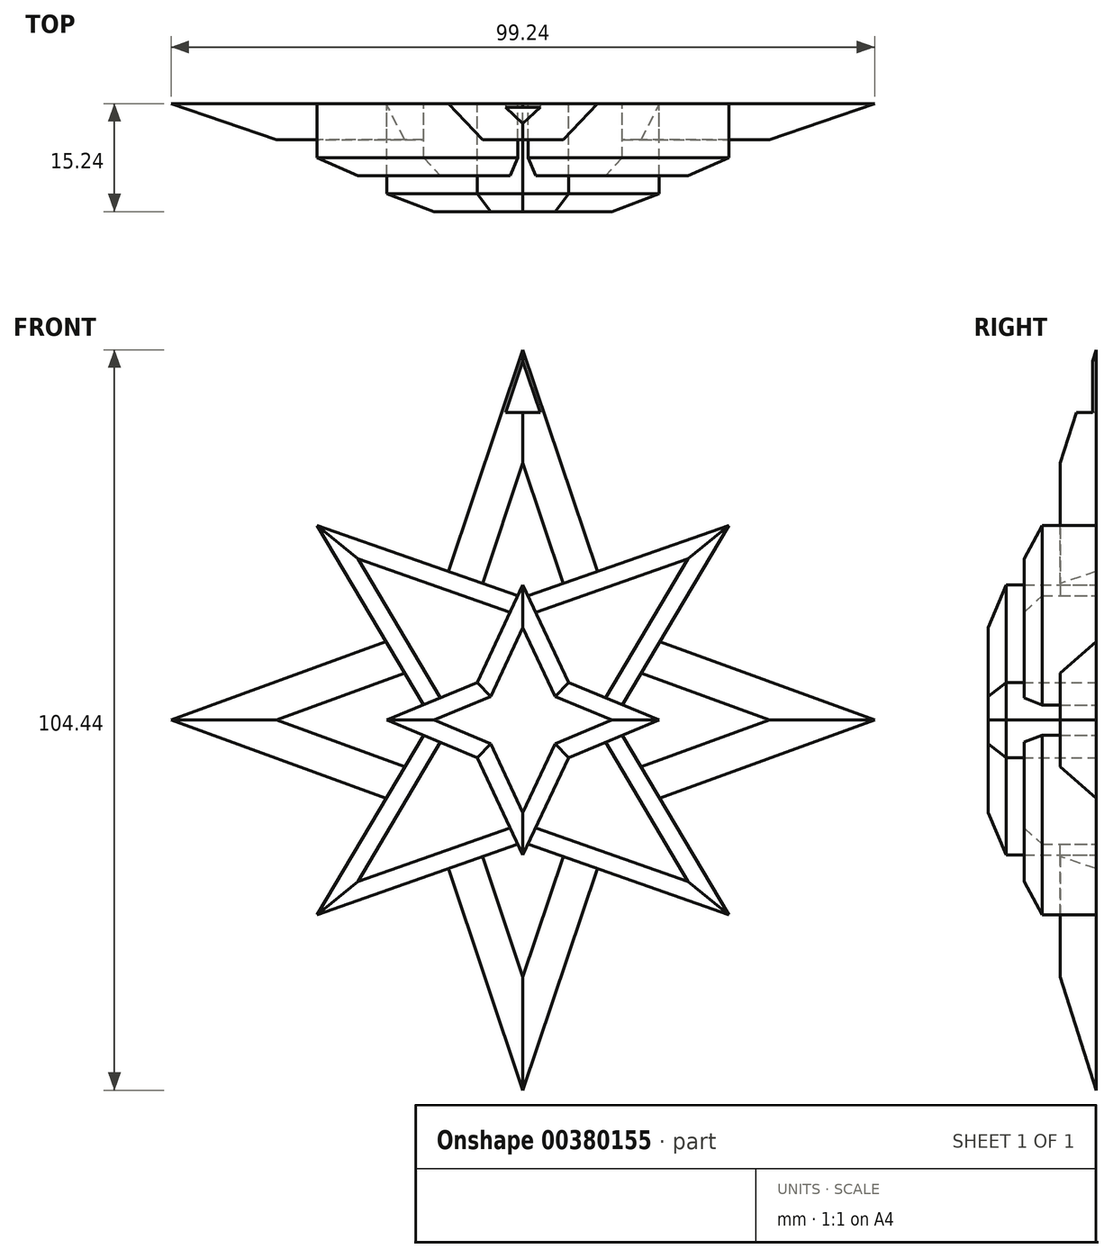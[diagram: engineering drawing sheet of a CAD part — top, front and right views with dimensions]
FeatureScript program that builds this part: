
annotation { "Feature Type Name" : "Feature", "Feature Type Description" : "" }
export const myFeature = defineFeature(function(context is Context, id is Id, definition is map)
    precondition{}
    {
        {
            var Q0;
            Q0=qCreatedBy(makeId("Front.planeOp"),FACE);
            var sketch = newSketch(context, id + "F0", { "sketchPlane" : qUnion([Q0])});
            skLineSegment(sketch, "E0", {"start": v(-49.62, 0) * mm, "end": v(-19.3, 11.04) * mm});
            skLineSegment(sketch, "E1", {"start": v(-19.3, 11.04) * mm, "end": v(-29.04, 27.46) * mm});
            skLineSegment(sketch, "E2", {"start": v(-29.04, 27.46) * mm, "end": v(-10.5, 20.95) * mm});
            skLineSegment(sketch, "E3", {"start": v(-10.5, 20.95) * mm, "end": v(0, 52.22) * mm});
            skLineSegment(sketch, "E4.MirrorCS", {"start": v(10.5, 20.95) * mm, "end": v(0, 52.22) * mm});
            skLineSegment(sketch, "E5.MirrorCS", {"start": v(29.04, 27.46) * mm, "end": v(10.5, 20.95) * mm});
            skLineSegment(sketch, "E6.MirrorCS", {"start": v(19.3, 11.04) * mm, "end": v(29.04, 27.46) * mm});
            skLineSegment(sketch, "E7.MirrorCS", {"start": v(49.62, 0) * mm, "end": v(19.3, 11.04) * mm});
            skLineSegment(sketch, "E8.MirrorCS", {"start": v(-49.62, 0) * mm, "end": v(-19.3, -11.04) * mm});
            skLineSegment(sketch, "E9.MirrorCS", {"start": v(-19.3, -11.04) * mm, "end": v(-29.04, -27.46) * mm});
            skLineSegment(sketch, "E10.MirrorCS", {"start": v(-29.04, -27.46) * mm, "end": v(-10.5, -20.95) * mm});
            skLineSegment(sketch, "E11.MirrorCS", {"start": v(-10.5, -20.95) * mm, "end": v(0, -52.22) * mm});
            skLineSegment(sketch, "E12.MirrorCS", {"start": v(10.5, -20.95) * mm, "end": v(0, -52.22) * mm});
            skLineSegment(sketch, "E13.MirrorCS", {"start": v(29.04, -27.46) * mm, "end": v(10.5, -20.95) * mm});
            skLineSegment(sketch, "E14.MirrorCS", {"start": v(19.3, -11.04) * mm, "end": v(29.04, -27.46) * mm});
            skLineSegment(sketch, "E15.MirrorCS", {"start": v(49.62, 0) * mm, "end": v(19.3, -11.04) * mm});
            skLineSegment(sketch, "E16", {"start": v(0, 19.05) * mm, "end": v(-6.42, 5.3) * mm});
            skLineSegment(sketch, "E17", {"start": v(-6.42, 5.3) * mm, "end": v(-19.2, 0) * mm});
            skLineSegment(sketch, "E18.MirrorCS", {"start": v(6.42, 5.3) * mm, "end": v(19.2, 0) * mm});
            skLineSegment(sketch, "E19.MirrorCS", {"start": v(0, 19.05) * mm, "end": v(6.42, 5.3) * mm});
            skLineSegment(sketch, "E20.MirrorCS", {"start": v(6.42, -5.3) * mm, "end": v(19.2, 0) * mm});
            skLineSegment(sketch, "E21.MirrorCS", {"start": v(0, -19.05) * mm, "end": v(6.42, -5.3) * mm});
            skLineSegment(sketch, "E22.MirrorCS", {"start": v(0, -19.05) * mm, "end": v(-6.42, -5.3) * mm});
            skLineSegment(sketch, "E23.MirrorCS", {"start": v(-6.42, -5.3) * mm, "end": v(-19.2, 0) * mm});
            skLineSegment(sketch, "E24", {"start": v(-19.3, 11.04) * mm, "end": v(-14.03, 2.14) * mm});
            skLineSegment(sketch, "E25", {"start": v(-10.5, 20.95) * mm, "end": v(-0.71, 17.52) * mm});
            skLineSegment(sketch, "E26", {"start": v(-19.3, -11.04) * mm, "end": v(-14.03, -2.14) * mm});
            skLineSegment(sketch, "E27", {"start": v(-10.5, -20.95) * mm, "end": v(-0.71, -17.52) * mm});
            skLineSegment(sketch, "E28", {"start": v(10.5, 20.95) * mm, "end": v(0.71, 17.52) * mm});
            skLineSegment(sketch, "E29", {"start": v(19.3, 11.04) * mm, "end": v(14.03, 2.14) * mm});
            skLineSegment(sketch, "E30", {"start": v(10.5, -20.95) * mm, "end": v(0.71, -17.52) * mm});
            skLineSegment(sketch, "E31", {"start": v(19.3, -11.04) * mm, "end": v(14.03, -2.14) * mm});
            skLineSegment(sketch, "E32", {"start": v(-49.62, 0) * mm, "end": v(-19.2, 0) * mm});
            skLineSegment(sketch, "E33", {"start": v(0, 19.05) * mm, "end": v(0, 52.22) * mm});
            skLineSegment(sketch, "E34", {"start": v(19.2, 0) * mm, "end": v(49.62, 0) * mm});
            skLineSegment(sketch, "E35", {"start": v(0, -19.05) * mm, "end": v(0, -52.22) * mm});
            skSolve(sketch);
        }
        {
            var Q0;
            Q0=makeQuery(id+"F0.imprint","IMPRINT",FACE,{"disambiguationData":[TD([[makeQuery(id+"F0.imprint","IMPRINT",EDGE,{"derivedFrom":sQuery(id+"F0.wireOp",EDGE,"E8.MirrorCS")}),1.0]])]});
            var Q1;
            Q1=makeQuery(id+"F0.imprint","IMPRINT",FACE,{"disambiguationData":[TD([[makeQuery(id+"F0.imprint","IMPRINT",EDGE,{"derivedFrom":sQuery(id+"F0.wireOp",EDGE,"E0")}),-1.0]])]});
            var Q2;
            Q2=makeQuery(id+"F0.imprint","IMPRINT",FACE,{"disambiguationData":[TD([[makeQuery(id+"F0.imprint","IMPRINT",EDGE,{"derivedFrom":sQuery(id+"F0.wireOp",EDGE,"E4.MirrorCS")}),1.0]])]});
            var Q3;
            Q3=makeQuery(id+"F0.imprint","IMPRINT",FACE,{"disambiguationData":[TD([[makeQuery(id+"F0.imprint","IMPRINT",EDGE,{"derivedFrom":sQuery(id+"F0.wireOp",EDGE,"E7.MirrorCS")}),1.0]])]});
            var Q4;
            Q4=makeQuery(id+"F0.imprint","IMPRINT",FACE,{"disambiguationData":[TD([[makeQuery(id+"F0.imprint","IMPRINT",EDGE,{"derivedFrom":sQuery(id+"F0.wireOp",EDGE,"E15.MirrorCS")}),-1.0]])]});
            var Q5;
            Q5=makeQuery(id+"F0.imprint","IMPRINT",FACE,{"disambiguationData":[TD([[makeQuery(id+"F0.imprint","IMPRINT",EDGE,{"derivedFrom":sQuery(id+"F0.wireOp",EDGE,"E3")}),-1.0]])]});
            var Q6;
            Q6=makeQuery(id+"F0.imprint","IMPRINT",FACE,{"disambiguationData":[TD([[makeQuery(id+"F0.imprint","IMPRINT",EDGE,{"derivedFrom":sQuery(id+"F0.wireOp",EDGE,"E12.MirrorCS")}),-1.0]])]});
            var Q7;
            Q7=makeQuery(id+"F0.imprint","IMPRINT",FACE,{"disambiguationData":[TD([[makeQuery(id+"F0.imprint","IMPRINT",EDGE,{"derivedFrom":sQuery(id+"F0.wireOp",EDGE,"E11.MirrorCS")}),1.0]])]});
            extrude(context, id + "F1", {"entities" : qUnion([Q0, Q1, Q2, Q3, Q4, Q5, Q6, Q7]), "depth" : 5.08 * mm});
        }
        {
            var Q0;
            Q0=makeQuery(id+"F0.imprint","IMPRINT",FACE,{"disambiguationData":[TD([[makeQuery(id+"F0.imprint","IMPRINT",EDGE,{"derivedFrom":sQuery(id+"F0.wireOp",EDGE,"E1")}),-1.0]])]});
            var Q1;
            Q1=makeQuery(id+"F0.imprint","IMPRINT",FACE,{"disambiguationData":[TD([[makeQuery(id+"F0.imprint","IMPRINT",EDGE,{"derivedFrom":sQuery(id+"F0.wireOp",EDGE,"E9.MirrorCS")}),1.0]])]});
            var Q2;
            Q2=makeQuery(id+"F0.imprint","IMPRINT",FACE,{"disambiguationData":[TD([[makeQuery(id+"F0.imprint","IMPRINT",EDGE,{"derivedFrom":sQuery(id+"F0.wireOp",EDGE,"E13.MirrorCS")}),-1.0]])]});
            var Q3;
            Q3=makeQuery(id+"F0.imprint","IMPRINT",FACE,{"disambiguationData":[TD([[makeQuery(id+"F0.imprint","IMPRINT",EDGE,{"derivedFrom":sQuery(id+"F0.wireOp",EDGE,"E5.MirrorCS")}),1.0]])]});
            extrude(context, id + "F2", {"entities" : qUnion([Q0, Q1, Q2, Q3]), "depth" : 10.16 * mm});
        }
        {
            var Q0;
            {var subQ9=sQuery(id+"F0.wireOp",EDGE,"E16");var subQ13=sQuery(id+"F0.wireOp",EDGE,"E17");var subQ14=makeQuery(id+"F0.imprint","INTERSECT",VERTEX,{"derivedFrom":[subQ9,subQ13]});Q0=makeQuery(id+"F0.imprint","IMPRINT",FACE,{"disambiguationData":[TD([[makeQuery(id+"F0.imprint","IMPRINT",EDGE,{"disambiguationData":[TD([[subQ14,1.0]])],"derivedFrom":subQ9}),1.0]])]});}
            extrude(context, id + "F3", {"entities" : qUnion([Q0]), "depth" : 15.24 * mm});
        }
        {
            var Q0;
            Q0=makeQuery(id+"F1.opExtrude","CAP_FACE",FACE,{"disambiguationData":[OSD([sQuery(id+"F0.wireOp",EDGE,"E3"),sQuery(id+"F0.wireOp",EDGE,"E4.MirrorCS"),sQuery(id+"F0.wireOp",EDGE,"E16"),sQuery(id+"F0.wireOp",EDGE,"E19.MirrorCS"),sQuery(id+"F0.wireOp",EDGE,"E25"),sQuery(id+"F0.wireOp",EDGE,"E28")])],"isStart":false});
            var sketch = newSketch(context, id + "F4", { "sketchPlane" : qUnion([Q0])});
            skLineSegment(sketch, "E36", {"start": v(0, 50.61) * mm, "end": v(-2.43, 43.39) * mm});
            skLineSegment(sketch, "E37.MirrorCS", {"start": v(0, 50.61) * mm, "end": v(2.43, 43.39) * mm});
            skLineSegment(sketch, "E38", {"start": v(-2.43, 43.39) * mm, "end": v(2.43, 43.39) * mm});
            skSolve(sketch);
        }
        {
            var Q0;
            Q0 = qSketchRegion(id + "F4", true);
            extrude(context, id + "F5", {"entities" : qUnion([Q0]), "operationType" : NewBodyOperationType.REMOVE, "oppositeDirection" : true, "depth" : 25.4 * mm});
        }
        {
            var Q0;
            Q0=makeQuery(id+"F2.opExtrude","CAP_EDGE",EDGE,{"disambiguationData":[OSD([sQuery(id+"F0.wireOp",EDGE,"E9.MirrorCS"),sQuery(id+"F0.wireOp",EDGE,"E26")])],"isStart":false});
            var Q1;
            Q1=makeQuery(id+"F2.opExtrude","CAP_EDGE",EDGE,{"disambiguationData":[OSD([sQuery(id+"F0.wireOp",EDGE,"E10.MirrorCS"),sQuery(id+"F0.wireOp",EDGE,"E27")])],"isStart":false});
            var Q2;
            Q2=makeQuery(id+"F2.opExtrude","CAP_EDGE",EDGE,{"disambiguationData":[OSD([sQuery(id+"F0.wireOp",EDGE,"E13.MirrorCS"),sQuery(id+"F0.wireOp",EDGE,"E30")])],"isStart":false});
            var Q3;
            Q3=makeQuery(id+"F2.opExtrude","CAP_EDGE",EDGE,{"disambiguationData":[OSD([sQuery(id+"F0.wireOp",EDGE,"E14.MirrorCS"),sQuery(id+"F0.wireOp",EDGE,"E31")])],"isStart":false});
            var Q4;
            Q4=makeQuery(id+"F2.opExtrude","CAP_EDGE",EDGE,{"disambiguationData":[OSD([sQuery(id+"F0.wireOp",EDGE,"E6.MirrorCS"),sQuery(id+"F0.wireOp",EDGE,"E29")])],"isStart":false});
            var Q5;
            Q5=makeQuery(id+"F2.opExtrude","CAP_EDGE",EDGE,{"disambiguationData":[OSD([sQuery(id+"F0.wireOp",EDGE,"E5.MirrorCS"),sQuery(id+"F0.wireOp",EDGE,"E28")])],"isStart":false});
            var Q6;
            Q6=makeQuery(id+"F2.opExtrude","CAP_EDGE",EDGE,{"disambiguationData":[OSD([sQuery(id+"F0.wireOp",EDGE,"E2"),sQuery(id+"F0.wireOp",EDGE,"E25")])],"isStart":false});
            var Q7;
            Q7=makeQuery(id+"F2.opExtrude","CAP_EDGE",EDGE,{"disambiguationData":[OSD([sQuery(id+"F0.wireOp",EDGE,"E1"),sQuery(id+"F0.wireOp",EDGE,"E24")])],"isStart":false});
            var Q8;
            Q8=makeQuery(id+"F3.opExtrude","CAP_EDGE",EDGE,{"disambiguationData":[OSD([sQuery(id+"F0.wireOp",EDGE,"E22.MirrorCS")])],"isStart":false});
            var Q9;
            Q9=makeQuery(id+"F3.opExtrude","CAP_EDGE",EDGE,{"disambiguationData":[OSD([sQuery(id+"F0.wireOp",EDGE,"E21.MirrorCS")])],"isStart":false});
            var Q10;
            Q10=makeQuery(id+"F3.opExtrude","CAP_EDGE",EDGE,{"disambiguationData":[OSD([sQuery(id+"F0.wireOp",EDGE,"E20.MirrorCS")])],"isStart":false});
            var Q11;
            Q11=makeQuery(id+"F3.opExtrude","CAP_EDGE",EDGE,{"disambiguationData":[OSD([sQuery(id+"F0.wireOp",EDGE,"E18.MirrorCS")])],"isStart":false});
            var Q12;
            Q12=makeQuery(id+"F3.opExtrude","CAP_EDGE",EDGE,{"disambiguationData":[OSD([sQuery(id+"F0.wireOp",EDGE,"E19.MirrorCS")])],"isStart":false});
            var Q13;
            Q13=makeQuery(id+"F3.opExtrude","CAP_EDGE",EDGE,{"disambiguationData":[OSD([sQuery(id+"F0.wireOp",EDGE,"E16")])],"isStart":false});
            var Q14;
            Q14=makeQuery(id+"F3.opExtrude","CAP_EDGE",EDGE,{"disambiguationData":[OSD([sQuery(id+"F0.wireOp",EDGE,"E17")])],"isStart":false});
            var Q15;
            Q15=makeQuery(id+"F3.opExtrude","CAP_EDGE",EDGE,{"disambiguationData":[OSD([sQuery(id+"F0.wireOp",EDGE,"E23.MirrorCS")])],"isStart":false});
            chamfer(context, id + "F6", {"entities" : qUnion([Q0, Q1, Q2, Q3, Q4, Q5, Q6, Q7, Q8, Q9, Q10, Q11, Q12, Q13, Q14, Q15]), "width" : 2.54 * mm, "tangentPropagation" : true});
        }
        {
            var Q0;
            Q0=makeQuery(id+"F1.opExtrude","CAP_EDGE",EDGE,{"disambiguationData":[OSD([sQuery(id+"F0.wireOp",EDGE,"E12.MirrorCS")])],"isStart":false});
            var Q1;
            Q1=makeQuery(id+"F1.opExtrude","CAP_EDGE",EDGE,{"disambiguationData":[OSD([sQuery(id+"F0.wireOp",EDGE,"E11.MirrorCS")])],"isStart":false});
            var Q2;
            Q2=makeQuery(id+"F1.opExtrude","CAP_EDGE",EDGE,{"disambiguationData":[OSD([sQuery(id+"F0.wireOp",EDGE,"E8.MirrorCS")])],"isStart":false});
            var Q3;
            Q3=makeQuery(id+"F1.opExtrude","CAP_EDGE",EDGE,{"disambiguationData":[OSD([sQuery(id+"F0.wireOp",EDGE,"E0")])],"isStart":false});
            var Q4;
            Q4=makeQuery(id+"F1.opExtrude","CAP_EDGE",EDGE,{"disambiguationData":[OSD([sQuery(id+"F0.wireOp",EDGE,"E7.MirrorCS")])],"isStart":false});
            var Q5;
            Q5=makeQuery(id+"F1.opExtrude","CAP_EDGE",EDGE,{"disambiguationData":[OSD([sQuery(id+"F0.wireOp",EDGE,"E15.MirrorCS")])],"isStart":false});
            var Q6;
            Q6=makeQuery(id+"F1.opExtrude","CAP_EDGE",EDGE,{"disambiguationData":[OSD([sQuery(id+"F0.wireOp",EDGE,"E4.MirrorCS")])],"isStart":false});
            var Q7;
            Q7=makeQuery(id+"F1.opExtrude","CAP_EDGE",EDGE,{"disambiguationData":[OSD([sQuery(id+"F0.wireOp",EDGE,"E3")])],"isStart":false});
            chamfer(context, id + "F7", {"entities" : qUnion([Q0, Q1, Q2, Q3, Q4, Q5, Q6, Q7]), "width" : 5.08 * mm, "tangentPropagation" : true});
        }
    });
